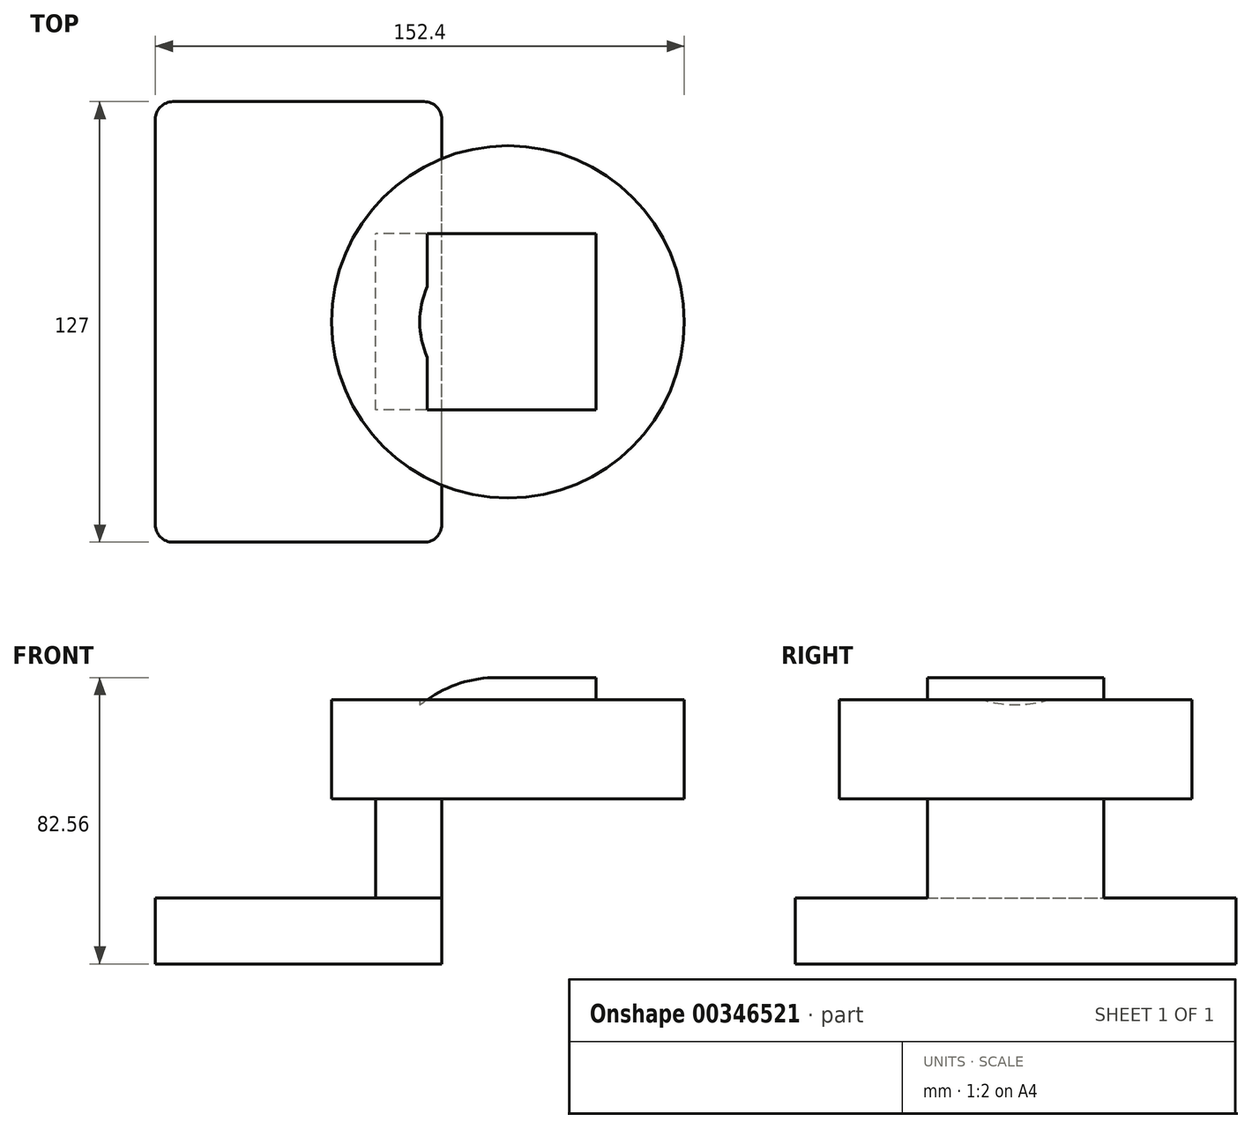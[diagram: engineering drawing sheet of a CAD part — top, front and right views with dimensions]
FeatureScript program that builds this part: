
annotation { "Feature Type Name" : "Feature", "Feature Type Description" : "" }
export const myFeature = defineFeature(function(context is Context, id is Id, definition is map)
    precondition{}
    {
        {
            var Q0;
            Q0=qCreatedBy(makeId("Front.planeOp"),FACE);
            var sketch = newSketch(context, id + "F0", { "sketchPlane" : qUnion([Q0])});
            skLineSegment(sketch, "E0.bottom", {"start": v(41.28, -9.52) * mm, "end": v(-41.28, -9.53) * mm});
            skLineSegment(sketch, "E0.top", {"start": v(41.27, 9.53) * mm, "end": v(-41.28, 9.53) * mm});
            skLineSegment(sketch, "E0.left", {"start": v(41.28, -9.52) * mm, "end": v(41.28, 9.53) * mm});
            skLineSegment(sketch, "E0.right", {"start": v(-41.28, -9.53) * mm, "end": v(-41.28, 9.53) * mm});
            skPoint(sketch, "E0.middle", {"position": v(0, 0) * mm});
            skLineSegment(sketch, "E1.bottom", {"start": v(111.12, 38.1) * mm, "end": v(60.32, 38.1) * mm});
            skLineSegment(sketch, "E1.top", {"start": v(111.12, 66.68) * mm, "end": v(60.33, 66.68) * mm});
            skLineSegment(sketch, "E1.left", {"start": v(111.12, 38.1) * mm, "end": v(111.12, 66.68) * mm});
            skLineSegment(sketch, "E1.right", {"start": v(60.32, 38.1) * mm, "end": v(60.32, 66.67) * mm});
            skPoint(sketch, "E1.middle", {"position": v(85.72, 52.39) * mm});
            skLineSegment(sketch, "E2", {"start": v(41.27, 9.53) * mm, "end": v(41.27, 38.1) * mm});
            skArc(sketch, "E3", {"start": v(41.27, 38.1) * mm, "mid": v(45.92, 49.33) * mm, "end": v(57.15, 53.98) * mm});
            skLineSegment(sketch, "E4", {"start": v(57.15, 53.98) * mm, "end": v(85.72, 53.98) * mm});
            skLineSegment(sketch, "E5.0", {"start": v(57.15, 73.03) * mm, "end": v(85.72, 73.03) * mm});
            skArc(sketch, "E5.1", {"start": v(22.23, 38.1) * mm, "mid": v(32.45, 62.8) * mm, "end": v(57.15, 73.03) * mm});
            skLineSegment(sketch, "E5.2", {"start": v(22.23, 9.53) * mm, "end": v(22.23, 38.1) * mm});
            skLineSegment(sketch, "E6", {"start": v(85.72, 73.03) * mm, "end": v(85.72, 53.98) * mm});
            skPoint(sketch, "E7", {"position": v(85.72, 66.68) * mm});
            skFitSpline(sketch, "E8", {"points": [v(-41.28, 9.53) * mm, v(57.15, 73.03) * mm], "startDerivative": vector(98.43, 63.5) * mm, "endDerivative": vector(96.32, -8.82) * mm});
            skSolve(sketch);
        }
        {
            var Q0;
            Q0=makeQuery(id+"F0.imprint","IMPRINT",FACE,{"disambiguationData":[TD([[makeQuery(id+"F0.imprint","IMPRINT",EDGE,{"derivedFrom":sQuery(id+"F0.wireOp",EDGE,"E0.bottom")}),-1.0]])]});
            extrude(context, id + "F1", {"entities" : qUnion([Q0]), "endBound" : BoundingType.SYMMETRIC, "depth" : 127 * mm});
        }
        {
            var Q0;
            {var subQ8=sQuery(id+"F0.wireOp",EDGE,"E2");Q0=makeQuery(id+"F0.imprint","IMPRINT",FACE,{"disambiguationData":[TD([[makeQuery(id+"F0.imprint","IMPRINT",EDGE,{"derivedFrom":subQ8}),1.0]])]});}
            var Q1;
            {var subQ0=sQuery(id+"F0.wireOp",EDGE,"E1.right");var subQ1=sQuery(id+"F0.wireOp",EDGE,"E1.top");var subQ2=makeQuery(id+"F0.imprint","INTERSECT",VERTEX,{"derivedFrom":[subQ1,subQ0]});Q1=makeQuery(id+"F0.imprint","IMPRINT",FACE,{"disambiguationData":[TD([[makeQuery(id+"F0.imprint","IMPRINT",EDGE,{"disambiguationData":[TD([[subQ2,1.0]])],"derivedFrom":subQ1}),1.0]])]});}
            extrude(context, id + "F2", {"entities" : qUnion([Q0, Q1]), "operationType" : NewBodyOperationType.ADD, "endBound" : BoundingType.SYMMETRIC, "depth" : 50.8 * mm});
        }
        {
            var Q0;
            Q0=makeQuery(id+"F0.imprint","IMPRINT",FACE,{"disambiguationData":[TD([[makeQuery(id+"F0.imprint","IMPRINT",EDGE,{"derivedFrom":sQuery(id+"F0.wireOp",EDGE,"E5.1")}),1.0]])]});
            extrude(context, id + "F3", {"entities" : qUnion([Q0]), "operationType" : NewBodyOperationType.ADD, "depth" : 15.88 * mm});
        }
        {
            var Q0;
            {var subQ1=sQuery(id+"F0.wireOp",EDGE,"E1.bottom");Q0=makeQuery(id+"F0.imprint","IMPRINT",FACE,{"disambiguationData":[TD([[makeQuery(id+"F0.imprint","IMPRINT",EDGE,{"derivedFrom":subQ1}),-1.0]])]});}
            var Q1;
            Q1=sQuery(id+"F0.wireOp",EDGE,"E1.right");
            revolve(context, id + "F4", {"operationType" : NewBodyOperationType.ADD, "entities" : qUnion([Q0]), "axis" : qUnion([Q1]), "revolveType" : RevolveType.FULL});
        }
        {
            var Q0;
            Q0=makeQuery(id+"F1.opExtrude","CAP_EDGE",EDGE,{"disambiguationData":[OSD([sQuery(id+"F0.wireOp",EDGE,"E0.left")])],"isStart":false});
            var Q1;
            Q1=makeQuery(id+"F1.opExtrude","CAP_EDGE",EDGE,{"disambiguationData":[OSD([sQuery(id+"F0.wireOp",EDGE,"E0.right")])],"isStart":false});
            var Q2;
            Q2=makeQuery(id+"F1.opExtrude","CAP_EDGE",EDGE,{"disambiguationData":[OSD([sQuery(id+"F0.wireOp",EDGE,"E0.left")])],"isStart":true});
            var Q3;
            Q3=makeQuery(id+"F1.opExtrude","CAP_EDGE",EDGE,{"disambiguationData":[OSD([sQuery(id+"F0.wireOp",EDGE,"E0.right")])],"isStart":true});
            fillet(context, id + "F5", {"entities" : qUnion([Q0, Q1, Q2, Q3]), "radius" : 5.08 * mm, "tangentPropagation" : true, "allowEdgeOverflow" : false});
        }
    });
